# Revit family: Plymold-Aurora-Outdoor_Table-With_Base
name_source: partatom
category: Furniture
units: mm (PartAtom-declared; Revit-internal decimal feet)

## family parameters
Always vertical = Yes
Cut with Voids When Loaded = No
OmniClass Number = 23.40.20.00
OmniClass Title = General Furniture and Specialties
Render Appearance Source = Family Geometry
Room Calculation Point = No
Shared = No
Work Plane-Based = No

## types (8) — shared parameters
Assembly Code = E2020200
Default Elevation = 0"
Height = 30"
Keynote = 12500
Manufacturer = Plymold Inc.
Product Documentation Link = https://plymold.com
Revit File Built By = https://servex-us.com
Sustainability = https://plymold.com
TOP MATERIAL = PLY - Sand
Type Comments = Aurora
URL = https://plymold.com

## per-type parameters (varying)
| type | Depth | Description | FRAME MATERIAL | Frame | Top | Width |
| 260300PL02KT | 26" | Outdoor Table With Base -  Iron Glimme - 30"W x 26"D | PLY - Iron Glimme Powdercoat | Plymold-Aurora-Dining_Height-Table_Base : 70609AL02 | Plymold-Aurora-Outdoor_Table : 260300PL02 | 30" |
| 260300PL03KT | 26" | Outdoor Table With Base -  Onyx Black - 30"W x 26"D | PLY - Onyx Black Powdercoat | Plymold-Aurora-Dining_Height-Table_Base : 70609AL03 | Plymold-Aurora-Outdoor_Table : 260300PL03 | 30" |
| 260440PL02KT | 26" | Outdoor Table With Base - Iron Glimme - 44"W x 26"D | PLY - Iron Glimme Powdercoat | Plymold-Aurora-Dining_Height-Table_Base : 70609AL02 | Plymold-Aurora-Outdoor_Table : 260440PL02 | 44" |
| 260440PL03KT | 26" | Outdoor Table With Base - Onyx Black - 44"W x 26"D | PLY - Onyx Black Powdercoat | Plymold-Aurora-Dining_Height-Table_Base : 70609AL03 | Plymold-Aurora-Outdoor_Table : 260440PL03 | 44" |
| 375375PL02KT | 37 1/2" | Outdoor Table With Base - Iron Glimme - 37.5"W x 37.5"D | PLY - Iron Glimme Powdercoat | Plymold-Aurora-Dining_Height-Table_Base : 70609AL02 | Plymold-Aurora-Outdoor_Table : 375375PL02 | 37 1/2" |
| 375375PL03KT | 37 1/2" | Outdoor Table With Base - Onyx Black - 37.5"W x 37.5"D | PLY - Onyx Black Powdercoat | Plymold-Aurora-Dining_Height-Table_Base : 70609AL03 | Plymold-Aurora-Outdoor_Table : 375375PL03 | 37 1/2" |
| 375570PL02KT | 26" | Outdoor Table With Base -  Iron Glimme - 57"W x 37.5"D | PLY - Iron Glimme Powdercoat | Plymold-Aurora-Dining_Height-Table_Base : 70609AL02 | Plymold-Aurora-Outdoor_Table : 375570PL02 | 44" |
| 375570PL03KT | 37 1/2" | Outdoor Table With Base - Onyx Black - 57"W x 37.5"D | PLY - Onyx Black Powdercoat | Plymold-Aurora-Dining_Height-Table_Base : 70609AL03 | Plymold-Aurora-Outdoor_Table : 375570PL03 | 37 1/2" |

note: column(s) folded — value = type name in every type: Model

## geometry (parser evidence)
native form markers: Sweep x13
no freeform markers — native parametric forms only
